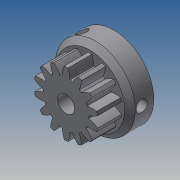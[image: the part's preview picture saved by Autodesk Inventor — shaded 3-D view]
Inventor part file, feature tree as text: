
AUTODESK INVENTOR PART (.ipt)
format: ipt  version: 2017 (Build 210142000, 142)  size: 305,664 bytes
history: native  units: mm
features: extrude x4, other x3, sketch x3, chamfer x2, pattern_circular x1, projected_geometry x1
ambient origin geometry x8: Origin, YZ Plane, XZ Plane, XY Plane, X Axis, Y Axis, Z Axis, Center Point
bodies: Body1 (feature_tree)
feature tree (14):
  other  "Sólido1"
  extrude  "Extrusión1"  Depth=11.85mm
  sketch  "Boceto2"  dims[d3=6.576542mm d4=3.3mm]
  extrude  "Extrusión2"  Depth=3.3mm
  extrude  "Extrusión3"  Depth=1.0mm
  extrude  "Extrusión4"  TaperAngle=120.0deg  [1 undecoded]
  other  "Dientes de engranaje recto3"
  pattern_circular  "Patrón circular1"  [2 undecoded]
  chamfer  "Chaflán1"  Distance=16.0mm
  chamfer  "Chaflán2"  Distance=4.0mm
  sketch  "Boceto1"  dims[d0=6.3mm d2=11.85mm]
  projected_geometry  "Contorno proyectado1"
  sketch  "Boceto3"  dims[d5=9.0mm d6=0.0mm d7=4.2mm d8=120.0deg d9=3.7mm d10=16.0mm d11=0.0mm d12=4.0mm d13=0.0mm d14=9.0mm d15=0.0mm d16=30.0mm d18=360.0deg d20=30.0mm d21=360.0deg d23=1.0mm d24=2.0mm d25=45.0deg d26=30.0mm d27=4.275mm d28=4.275mm d29=2.0mm d30=2.0mm d31=45.0deg]
  other  "iFeature1:3"
note: 3 required parameter values undecoded (feature->parameter linkage not recoverable at this tier; creation-order binding heuristic only, values carry confidence <= 0.55)
